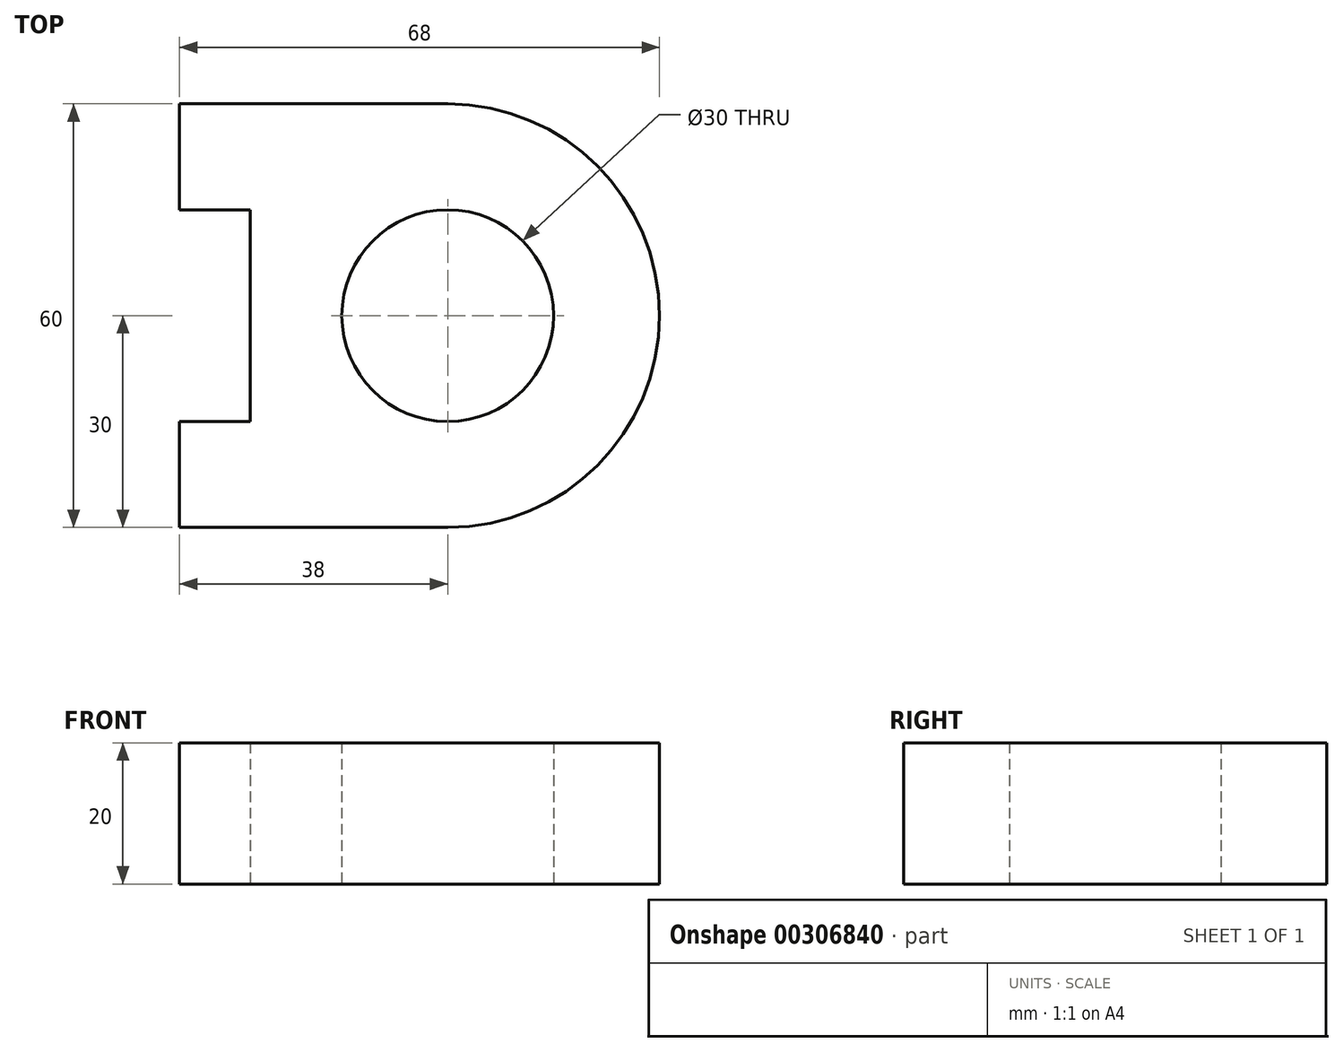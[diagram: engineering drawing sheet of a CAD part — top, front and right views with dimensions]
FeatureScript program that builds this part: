
annotation { "Feature Type Name" : "Feature", "Feature Type Description" : "" }
export const myFeature = defineFeature(function(context is Context, id is Id, definition is map)
    precondition{}
    {
        {
            var Q0;
            Q0=qCreatedBy(makeId("Top.planeOp"),FACE);
            var sketch = newSketch(context, id + "F0", { "sketchPlane" : qUnion([Q0])});
            skCircle(sketch, "E0", {"center": v(0, 0) * mm, "radius": 15 * mm});
            skArc(sketch, "E1", {"start": v(0, -30) * mm, "mid": v(30, 0) * mm, "end": v(0, 30) * mm});
            skLineSegment(sketch, "E2", {"start": v(0, 30) * mm, "end": v(-38, 30) * mm});
            skLineSegment(sketch, "E3", {"start": v(-38, 30) * mm, "end": v(-38, 15) * mm});
            skLineSegment(sketch, "E4", {"start": v(-38, 15) * mm, "end": v(-28, 15) * mm});
            skLineSegment(sketch, "E5", {"start": v(-28, 15) * mm, "end": v(-28, -15) * mm});
            skLineSegment(sketch, "E6", {"start": v(-28, -15) * mm, "end": v(-38, -15) * mm});
            skLineSegment(sketch, "E7", {"start": v(-38, -15) * mm, "end": v(-38, -30) * mm});
            skLineSegment(sketch, "E8", {"start": v(-38, -30) * mm, "end": v(0, -30) * mm});
            skSolve(sketch);
        }
        {
            var Q0;
            Q0 = qSketchRegion(id + "F0", true);
            extrude(context, id + "F1", {"entities" : qUnion([Q0]), "endBound" : BoundingType.SYMMETRIC, "depth" : 20 * mm});
        }
    });
